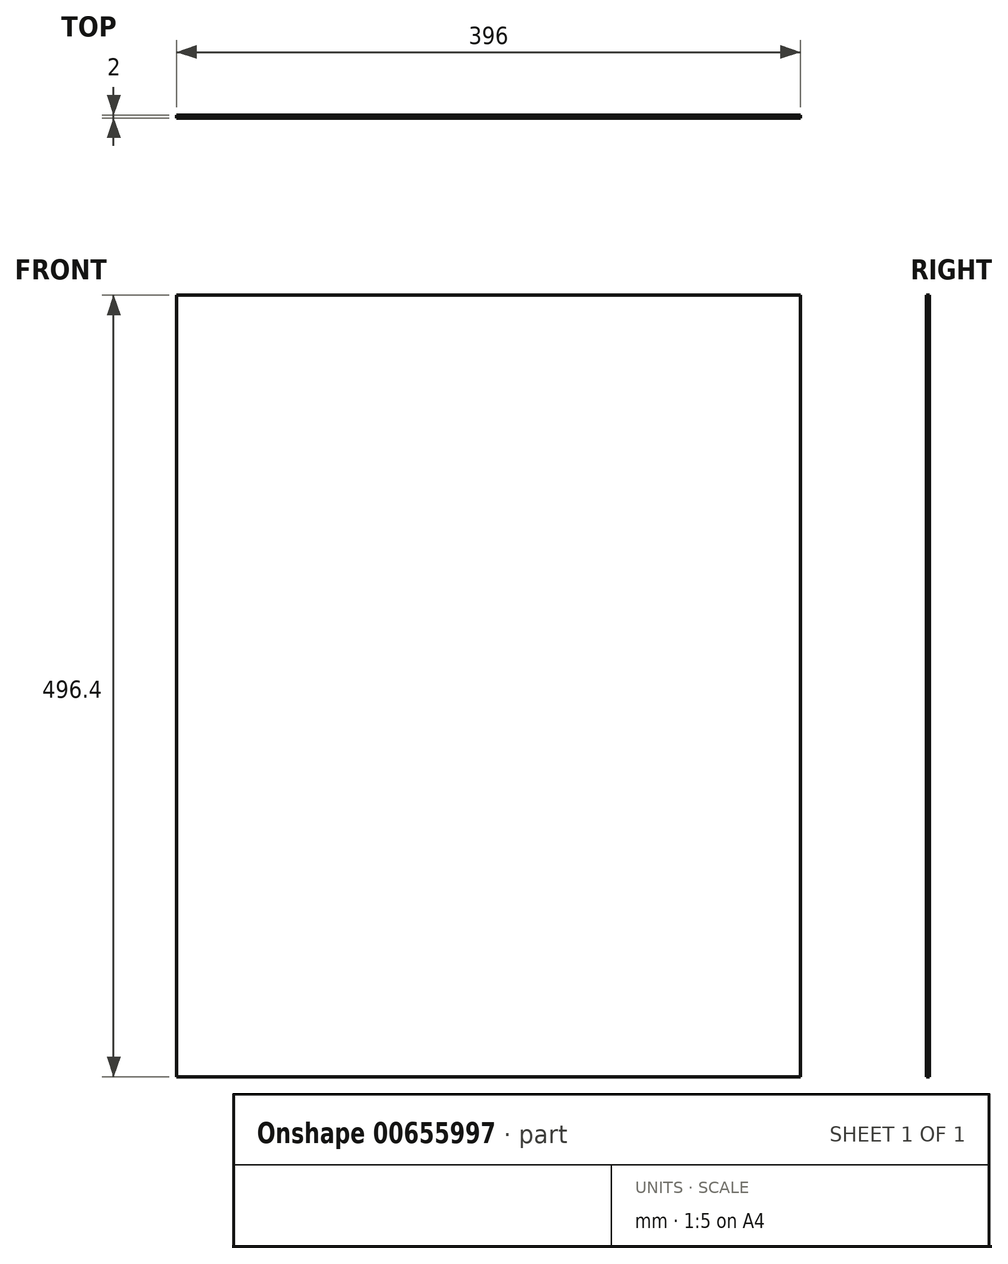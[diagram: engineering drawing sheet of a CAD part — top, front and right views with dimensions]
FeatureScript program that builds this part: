
annotation { "Feature Type Name" : "Feature", "Feature Type Description" : "" }
export const myFeature = defineFeature(function(context is Context, id is Id, definition is map)
    precondition{}
    {
        {
            var Q0;
            Q0=qCreatedBy(makeId("Front.planeOp"),FACE);
            var sketch = newSketch(context, id + "F0", { "sketchPlane" : qUnion([Q0])});
            skPoint(sketch, "E0.middle", {"position": v(0, 0) * mm});
            skLineSegment(sketch, "E1.bottom", {"start": v(-199, 347.15) * mm, "end": v(197, 347.15) * mm});
            skLineSegment(sketch, "E1.top", {"start": v(-199, -149.25) * mm, "end": v(197, -149.25) * mm});
            skLineSegment(sketch, "E1.left", {"start": v(-199, 347.15) * mm, "end": v(-199, -149.25) * mm});
            skLineSegment(sketch, "E1.right", {"start": v(197, 347.15) * mm, "end": v(197, -149.25) * mm});
            skSolve(sketch);
        }
        {
            var Q0;
            Q0=makeQuery(id+"F0.imprint","IMPRINT",FACE,{"disambiguationData":[TD([[makeQuery(id+"F0.imprint","IMPRINT",EDGE,{"derivedFrom":sQuery(id+"F0.wireOp",EDGE,"E1.bottom")}),-1.0]])]});
            extrude(context, id + "F1", {"entities" : qUnion([Q0]), "depth" : 2 * mm, "offsetDistance" : 25.4 * mm});
        }
    });
